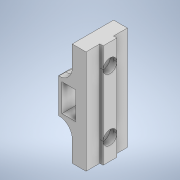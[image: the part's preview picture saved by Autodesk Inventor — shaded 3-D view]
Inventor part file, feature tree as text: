
AUTODESK INVENTOR PART (.ipt)
format: ipt  version: 2020 (Build 240168000, 168)  size: 250,880 bytes
history: native  units: in
note: dims shown in document units (in); Inventor stores cm internally (conversion verified against a paired STEP export)
features: sketch x5, extrude x4, other x2, hole x1, fillet x1
ambient origin geometry x8: Origin, YZ Plane, XZ Plane, XY Plane, X Axis, Y Axis, Z Axis, Center Point
bodies: Solid1 (feature_tree)
feature tree (13):
  other  "Annotations"
  extrude  "Extrusion1"  Depth=0.6in
  hole  "Hole1"  [1 undecoded]
  extrude  "Extrusion2"  Depth=0.1in
  extrude  "Extrusion3"  Depth=0.1in
  extrude  "Extrusion4"  Depth=0.195in
  fillet  "Fillet1"  Radius=0.3in
  sketch  "Sketch1"  dims[d0=0.2in d1=0.6in]
  sketch  "Sketch2"  dims[d2=0.1in d3=0.15in]
  sketch  "Sketch3"  dims[d4=0.1in d5=0.1in]
  sketch  "Sketch4"  dims[d6=0.2in d7=0.1in]
  sketch  "Sketch5"  dims[d8=1.5in d9=0.0in d10=0.3in d11=0.3in d12=0.2in d13=0.75in d14=0.4in d15=0.15in d16=0.5635in d17=1.0in d18=0.8108in d19=0.5in d20=0.5in d21=0.2in d22=0.0in d23=0.05in d24=0.05in d25=0.2in d26=0.4in d27=0.6in d28=0.0in d32=0.248in d33=1.5in d34=0.0in d35=0.195in d29=0.1606in d30=0.1409in d31=0.05in]
  other  "Linear Dimension 1"
note: 1 required parameter value undecoded (feature->parameter linkage not recoverable at this tier; creation-order binding heuristic only, values carry confidence <= 0.55)
